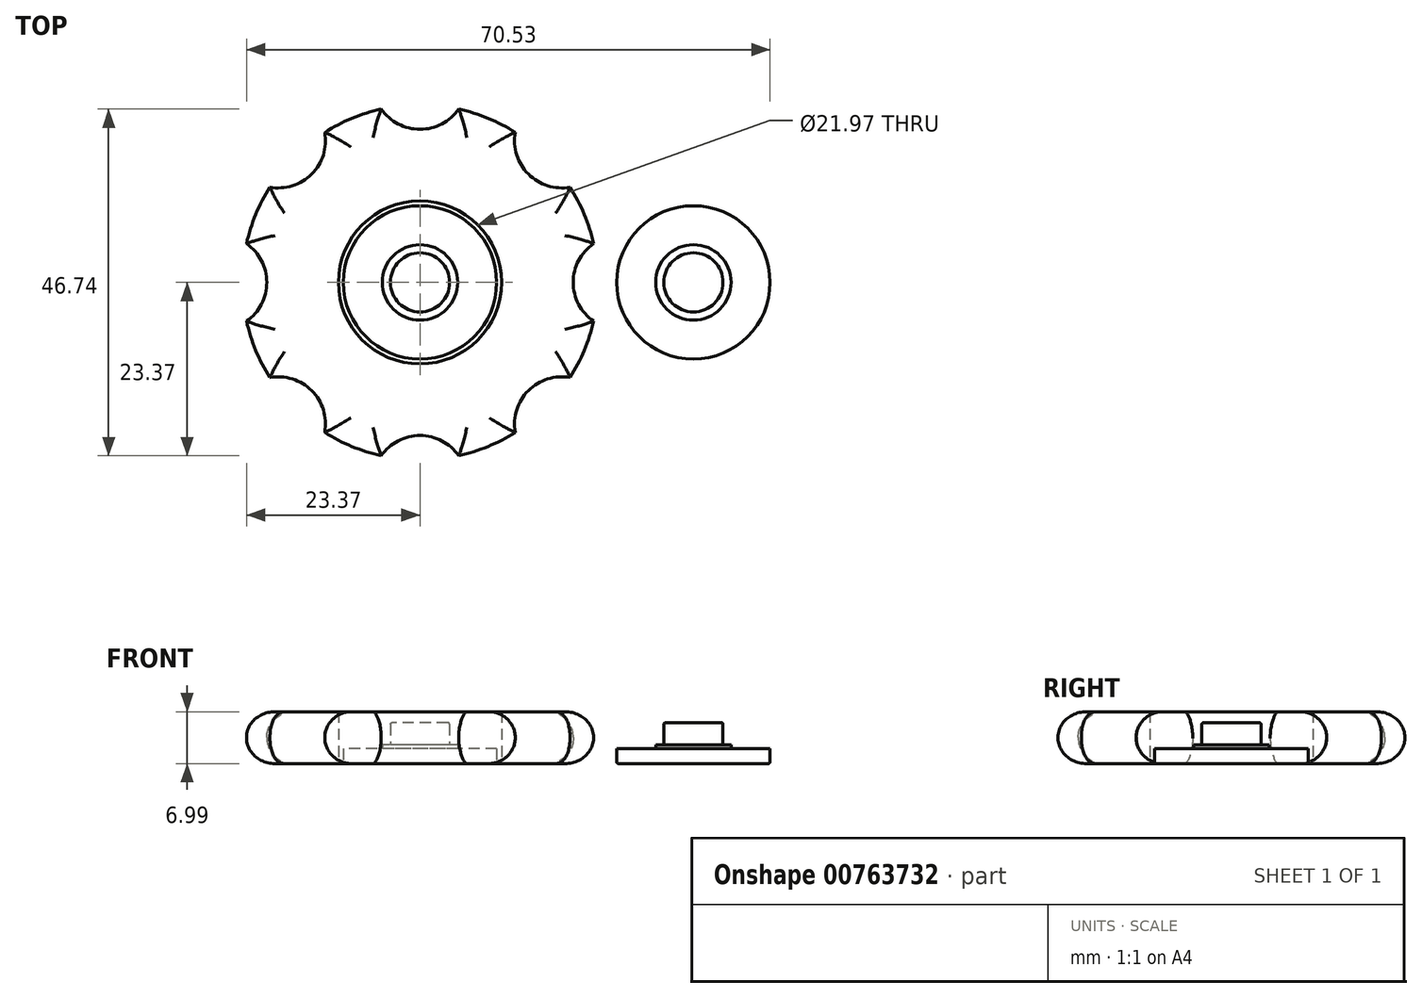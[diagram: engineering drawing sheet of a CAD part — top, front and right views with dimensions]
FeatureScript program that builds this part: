
annotation { "Feature Type Name" : "Feature", "Feature Type Description" : "" }
export const myFeature = defineFeature(function(context is Context, id is Id, definition is map)
    precondition{}
    {
        {
            var Q0;
            Q0=qCreatedBy(makeId("Top.planeOp"),FACE);
            var sketch = newSketch(context, id + "F0", { "sketchPlane" : qUnion([Q0])});
            skCircle(sketch, "E0", {"center": v(0, 0) * mm, "radius": 10.99 * mm});
            skCircle(sketch, "E1", {"center": v(0, 0) * mm, "radius": 26.99 * mm});
            skPoint(sketch, "E2", {"position": v(0, 26.99) * mm});
            skPoint(sketch, "E3", {"position": v(0, -26.99) * mm});
            skPoint(sketch, "E4", {"position": v(-26.99, 0) * mm});
            skPoint(sketch, "E5", {"position": v(26.99, 0) * mm});
            skCircle(sketch, "E6", {"center": v(0, 26.99) * mm, "radius": 6.35 * mm});
            skCircle(sketch, "E7", {"center": v(19.08, 19.08) * mm, "radius": 6.35 * mm});
            skCircle(sketch, "E8", {"center": v(26.99, 0) * mm, "radius": 6.35 * mm});
            skCircle(sketch, "E9", {"center": v(-19.08, 19.08) * mm, "radius": 6.35 * mm});
            skCircle(sketch, "E10", {"center": v(-26.99, 0) * mm, "radius": 6.35 * mm});
            skCircle(sketch, "E11", {"center": v(-19.08, -19.08) * mm, "radius": 6.35 * mm});
            skCircle(sketch, "E12", {"center": v(0, -26.99) * mm, "radius": 6.35 * mm});
            skCircle(sketch, "E13", {"center": v(19.08, -19.08) * mm, "radius": 6.35 * mm});
            skCircle(sketch, "E14", {"center": v(0, 0) * mm, "radius": 23.95 * mm});
            skCircle(sketch, "E15", {"center": v(0, 0) * mm, "radius": 10.33 * mm});
            skCircle(sketch, "E16", {"center": v(0, 0) * mm, "radius": 5.08 * mm});
            skCircle(sketch, "E17", {"center": v(0, 0) * mm, "radius": 3.99 * mm});
            skSolve(sketch);
        }
        {
            var Q0;
            {var subQ1=sQuery(id+"F0.wireOp",EDGE,"vauF7w1j-dYiE-ONAp-yt3V-veebpfeqqCza");var subQ6=sQuery(id+"F0.wireOp",EDGE,"E0");var subQ11=makeQuery(id+"F0.imprint","INTERSECT",VERTEX,{"disambiguationData":[OD(0.0)],"derivedFrom":[subQ6,subQ1]});Q0=makeQuery(id+"F0.imprint","IMPRINT",FACE,{"disambiguationData":[TD([[makeQuery(id+"F0.imprint","IMPRINT",EDGE,{"disambiguationData":[TD([[subQ11,-1.0]])],"derivedFrom":subQ6}),-1.0]])]});}
            var Q1;
            {var subQ1=sQuery(id+"F0.wireOp",EDGE,"2xs85ny7-f9sM-EysO-I2VY-nclEqGJr2pPz");var subQ6=sQuery(id+"F0.wireOp",EDGE,"E0");var subQ10=makeQuery(id+"F0.imprint","INTERSECT",VERTEX,{"disambiguationData":[OD(0.0)],"derivedFrom":[subQ6,subQ1]});Q1=makeQuery(id+"F0.imprint","IMPRINT",FACE,{"disambiguationData":[TD([[makeQuery(id+"F0.imprint","IMPRINT",EDGE,{"disambiguationData":[TD([[subQ10,-1.0]])],"derivedFrom":subQ6}),-1.0]])]});}
            var Q2;
            {var subQ0=sQuery(id+"F0.wireOp",EDGE,"xx3eZdgf-G35K-R4WY-AsTk-CgdW70iCga0P");var subQ1=sQuery(id+"F0.wireOp",EDGE,"E0");var subQ2=makeQuery(id+"F0.imprint","INTERSECT",VERTEX,{"disambiguationData":[OD(0.0)],"derivedFrom":[subQ1,subQ0]});Q2=makeQuery(id+"F0.imprint","IMPRINT",FACE,{"disambiguationData":[TD([[makeQuery(id+"F0.imprint","IMPRINT",EDGE,{"disambiguationData":[TD([[subQ2,-1.0]])],"derivedFrom":subQ1}),-1.0]])]});}
            var Q3;
            {var subQ1=sQuery(id+"F0.wireOp",EDGE,"xx3eZdgf-G35K-R4WY-AsTk-CgdW70iCga0P");var subQ5=sQuery(id+"F0.wireOp",EDGE,"E0");var subQ6=makeQuery(id+"F0.imprint","INTERSECT",VERTEX,{"disambiguationData":[OD(0.0)],"derivedFrom":[subQ5,subQ1]});Q3=makeQuery(id+"F0.imprint","IMPRINT",FACE,{"disambiguationData":[TD([[makeQuery(id+"F0.imprint","IMPRINT",EDGE,{"disambiguationData":[TD([[subQ6,1.0]])],"derivedFrom":subQ5}),-1.0]])]});}
            var Q4;
            {var subQ1=sQuery(id+"F0.wireOp",EDGE,"aaSnfk4t-Vx8F-0rh1-x5wZ-IxOcUmj5yS2X");var subQ6=sQuery(id+"F0.wireOp",EDGE,"E0");var subQ10=makeQuery(id+"F0.imprint","INTERSECT",VERTEX,{"disambiguationData":[OD(0.0)],"derivedFrom":[subQ6,subQ1]});Q4=makeQuery(id+"F0.imprint","IMPRINT",FACE,{"disambiguationData":[TD([[makeQuery(id+"F0.imprint","IMPRINT",EDGE,{"disambiguationData":[TD([[subQ10,1.0]])],"derivedFrom":subQ6}),-1.0]])]});}
            var Q5;
            {var subQ1=sQuery(id+"F0.wireOp",EDGE,"2xs85ny7-f9sM-EysO-I2VY-nclEqGJr2pPz");var subQ5=sQuery(id+"F0.wireOp",EDGE,"E0");var subQ6=makeQuery(id+"F0.imprint","INTERSECT",VERTEX,{"disambiguationData":[OD(1.0)],"derivedFrom":[subQ5,subQ1]});Q5=makeQuery(id+"F0.imprint","IMPRINT",FACE,{"disambiguationData":[TD([[makeQuery(id+"F0.imprint","IMPRINT",EDGE,{"disambiguationData":[TD([[subQ6,-1.0]])],"derivedFrom":subQ5}),-1.0]])]});}
            var Q6;
            {var subQ1=sQuery(id+"F0.wireOp",EDGE,"xx3eZdgf-G35K-R4WY-AsTk-CgdW70iCga0P");var subQ5=sQuery(id+"F0.wireOp",EDGE,"E0");var subQ6=makeQuery(id+"F0.imprint","INTERSECT",VERTEX,{"disambiguationData":[OD(1.0)],"derivedFrom":[subQ5,subQ1]});Q6=makeQuery(id+"F0.imprint","IMPRINT",FACE,{"disambiguationData":[TD([[makeQuery(id+"F0.imprint","IMPRINT",EDGE,{"disambiguationData":[TD([[subQ6,-1.0]])],"derivedFrom":subQ5}),-1.0]])]});}
            var Q7;
            {var subQ1=sQuery(id+"F0.wireOp",EDGE,"aaSnfk4t-Vx8F-0rh1-x5wZ-IxOcUmj5yS2X");var subQ6=sQuery(id+"F0.wireOp",EDGE,"E0");var subQ10=makeQuery(id+"F0.imprint","INTERSECT",VERTEX,{"disambiguationData":[OD(1.0)],"derivedFrom":[subQ6,subQ1]});Q7=makeQuery(id+"F0.imprint","IMPRINT",FACE,{"disambiguationData":[TD([[makeQuery(id+"F0.imprint","IMPRINT",EDGE,{"disambiguationData":[TD([[subQ10,-1.0]])],"derivedFrom":subQ6}),-1.0]])]});}
            extrude(context, id + "F1", {"entities" : qUnion([Q0, Q1, Q2, Q3, Q4, Q5, Q6, Q7]), "depth" : 7 * mm, "offsetDistance" : 25.4 * mm});
        }
        {
            var Q0;
            Q0=makeQuery(id+"F1.opExtrude","CAP_EDGE",EDGE,{"disambiguationData":[OSD([sQuery(id+"F0.wireOp",EDGE,"E10")])],"isStart":false});
            var Q1;
            Q1=makeQuery(id+"F1.opExtrude","CAP_EDGE",EDGE,{"disambiguationData":[OSD([sQuery(id+"F0.wireOp",EDGE,"E9")])],"isStart":false});
            var Q2;
            Q2=makeQuery(id+"F1.opExtrude","CAP_EDGE",EDGE,{"disambiguationData":[OSD([sQuery(id+"F0.wireOp",EDGE,"E6")])],"isStart":false});
            var Q3;
            Q3=makeQuery(id+"F1.opExtrude","CAP_EDGE",EDGE,{"disambiguationData":[OSD([sQuery(id+"F0.wireOp",EDGE,"E7")])],"isStart":false});
            var Q4;
            Q4=makeQuery(id+"F1.opExtrude","CAP_EDGE",EDGE,{"disambiguationData":[OSD([sQuery(id+"F0.wireOp",EDGE,"E8")])],"isStart":false});
            var Q5;
            Q5=makeQuery(id+"F1.opExtrude","CAP_EDGE",EDGE,{"disambiguationData":[OSD([sQuery(id+"F0.wireOp",EDGE,"E13")])],"isStart":false});
            var Q6;
            Q6=makeQuery(id+"F1.opExtrude","CAP_EDGE",EDGE,{"disambiguationData":[OSD([sQuery(id+"F0.wireOp",EDGE,"E12")])],"isStart":false});
            var Q7;
            {var subQ0=sQuery(id+"F0.wireOp",EDGE,"E14");Q7=makeQuery(id+"F1.opExtrude","CAP_EDGE",EDGE,{"disambiguationData":[OSD([subQ0]),TDD([makeQuery(id+"F0.imprint","IMPRINT",EDGE,{"disambiguationData":[TD([[makeQuery(id+"F0.imprint","INTERSECT",VERTEX,{"disambiguationData":[OD(0.0)],"derivedFrom":[sQuery(id+"F0.wireOp",EDGE,"E12"),subQ0]}),-1.0]])],"derivedFrom":subQ0})])],"isStart":false});}
            var Q8;
            {var subQ0=sQuery(id+"F0.wireOp",EDGE,"E14");Q8=makeQuery(id+"F1.opExtrude","CAP_EDGE",EDGE,{"disambiguationData":[OSD([subQ0]),TDD([makeQuery(id+"F0.imprint","IMPRINT",EDGE,{"disambiguationData":[TD([[makeQuery(id+"F0.imprint","INTERSECT",VERTEX,{"disambiguationData":[OD(1.0)],"derivedFrom":[sQuery(id+"F0.wireOp",EDGE,"E11"),subQ0]}),-1.0]])],"derivedFrom":subQ0})])],"isStart":false});}
            var Q9;
            Q9=makeQuery(id+"F1.opExtrude","CAP_EDGE",EDGE,{"disambiguationData":[OSD([sQuery(id+"F0.wireOp",EDGE,"E11")])],"isStart":false});
            var Q10;
            {var subQ0=sQuery(id+"F0.wireOp",EDGE,"E14");Q10=makeQuery(id+"F1.opExtrude","CAP_EDGE",EDGE,{"disambiguationData":[OSD([subQ0]),TDD([makeQuery(id+"F0.imprint","IMPRINT",EDGE,{"disambiguationData":[TD([[makeQuery(id+"F0.imprint","INTERSECT",VERTEX,{"disambiguationData":[OD(1.0)],"derivedFrom":[sQuery(id+"F0.wireOp",EDGE,"E10"),subQ0]}),-1.0]])],"derivedFrom":subQ0})])],"isStart":false});}
            var Q11;
            {var subQ0=sQuery(id+"F0.wireOp",EDGE,"E14");Q11=makeQuery(id+"F1.opExtrude","CAP_EDGE",EDGE,{"disambiguationData":[OSD([subQ0]),TDD([makeQuery(id+"F0.imprint","IMPRINT",EDGE,{"disambiguationData":[TD([[makeQuery(id+"F0.imprint","INTERSECT",VERTEX,{"disambiguationData":[OD(1.0)],"derivedFrom":[sQuery(id+"F0.wireOp",EDGE,"E9"),subQ0]}),-1.0]])],"derivedFrom":subQ0})])],"isStart":false});}
            var Q12;
            {var subQ0=sQuery(id+"F0.wireOp",EDGE,"E14");Q12=makeQuery(id+"F1.opExtrude","CAP_EDGE",EDGE,{"disambiguationData":[OSD([subQ0]),TDD([makeQuery(id+"F0.imprint","IMPRINT",EDGE,{"disambiguationData":[TD([[makeQuery(id+"F0.imprint","INTERSECT",VERTEX,{"disambiguationData":[OD(0.0)],"derivedFrom":[sQuery(id+"F0.wireOp",EDGE,"E6"),subQ0]}),-1.0]])],"derivedFrom":subQ0})])],"isStart":false});}
            var Q13;
            {var subQ0=sQuery(id+"F0.wireOp",EDGE,"E14");Q13=makeQuery(id+"F1.opExtrude","CAP_EDGE",EDGE,{"disambiguationData":[OSD([subQ0]),TDD([makeQuery(id+"F0.imprint","IMPRINT",EDGE,{"disambiguationData":[TD([[makeQuery(id+"F0.imprint","INTERSECT",VERTEX,{"disambiguationData":[OD(1.0)],"derivedFrom":[sQuery(id+"F0.wireOp",EDGE,"E6"),subQ0]}),1.0]])],"derivedFrom":subQ0})])],"isStart":false});}
            var Q14;
            {var subQ0=sQuery(id+"F0.wireOp",EDGE,"E14");Q14=makeQuery(id+"F1.opExtrude","CAP_EDGE",EDGE,{"disambiguationData":[OSD([subQ0]),TDD([makeQuery(id+"F0.imprint","IMPRINT",EDGE,{"disambiguationData":[TD([[makeQuery(id+"F0.imprint","INTERSECT",VERTEX,{"disambiguationData":[OD(1.0)],"derivedFrom":[sQuery(id+"F0.wireOp",EDGE,"E7"),subQ0]}),1.0]])],"derivedFrom":subQ0})])],"isStart":false});}
            var Q15;
            {var subQ0=sQuery(id+"F0.wireOp",EDGE,"E14");Q15=makeQuery(id+"F1.opExtrude","CAP_EDGE",EDGE,{"disambiguationData":[OSD([subQ0]),TDD([makeQuery(id+"F0.imprint","IMPRINT",EDGE,{"disambiguationData":[TD([[makeQuery(id+"F0.imprint","INTERSECT",VERTEX,{"disambiguationData":[OD(1.0)],"derivedFrom":[sQuery(id+"F0.wireOp",EDGE,"E8"),subQ0]}),1.0]])],"derivedFrom":subQ0})])],"isStart":false});}
            var Q16;
            {var subQ0=sQuery(id+"F0.wireOp",EDGE,"E14");Q16=makeQuery(id+"F1.opExtrude","CAP_EDGE",EDGE,{"disambiguationData":[OSD([subQ0]),TDD([makeQuery(id+"F0.imprint","IMPRINT",EDGE,{"disambiguationData":[TD([[makeQuery(id+"F0.imprint","INTERSECT",VERTEX,{"disambiguationData":[OD(1.0)],"derivedFrom":[sQuery(id+"F0.wireOp",EDGE,"E11"),subQ0]}),-1.0]])],"derivedFrom":subQ0})])],"isStart":true});}
            var Q17;
            Q17=makeQuery(id+"F1.opExtrude","CAP_EDGE",EDGE,{"disambiguationData":[OSD([sQuery(id+"F0.wireOp",EDGE,"E11")])],"isStart":true});
            var Q18;
            {var subQ0=sQuery(id+"F0.wireOp",EDGE,"E14");Q18=makeQuery(id+"F1.opExtrude","CAP_EDGE",EDGE,{"disambiguationData":[OSD([subQ0]),TDD([makeQuery(id+"F0.imprint","IMPRINT",EDGE,{"disambiguationData":[TD([[makeQuery(id+"F0.imprint","INTERSECT",VERTEX,{"disambiguationData":[OD(1.0)],"derivedFrom":[sQuery(id+"F0.wireOp",EDGE,"E10"),subQ0]}),-1.0]])],"derivedFrom":subQ0})])],"isStart":true});}
            var Q19;
            Q19=makeQuery(id+"F1.opExtrude","CAP_EDGE",EDGE,{"disambiguationData":[OSD([sQuery(id+"F0.wireOp",EDGE,"E10")])],"isStart":true});
            var Q20;
            {var subQ0=sQuery(id+"F0.wireOp",EDGE,"E14");Q20=makeQuery(id+"F1.opExtrude","CAP_EDGE",EDGE,{"disambiguationData":[OSD([subQ0]),TDD([makeQuery(id+"F0.imprint","IMPRINT",EDGE,{"disambiguationData":[TD([[makeQuery(id+"F0.imprint","INTERSECT",VERTEX,{"disambiguationData":[OD(1.0)],"derivedFrom":[sQuery(id+"F0.wireOp",EDGE,"E9"),subQ0]}),-1.0]])],"derivedFrom":subQ0})])],"isStart":true});}
            var Q21;
            Q21=makeQuery(id+"F1.opExtrude","CAP_EDGE",EDGE,{"disambiguationData":[OSD([sQuery(id+"F0.wireOp",EDGE,"E9")])],"isStart":true});
            var Q22;
            {var subQ0=sQuery(id+"F0.wireOp",EDGE,"E14");Q22=makeQuery(id+"F1.opExtrude","CAP_EDGE",EDGE,{"disambiguationData":[OSD([subQ0]),TDD([makeQuery(id+"F0.imprint","IMPRINT",EDGE,{"disambiguationData":[TD([[makeQuery(id+"F0.imprint","INTERSECT",VERTEX,{"disambiguationData":[OD(0.0)],"derivedFrom":[sQuery(id+"F0.wireOp",EDGE,"E6"),subQ0]}),-1.0]])],"derivedFrom":subQ0})])],"isStart":true});}
            var Q23;
            Q23=makeQuery(id+"F1.opExtrude","CAP_EDGE",EDGE,{"disambiguationData":[OSD([sQuery(id+"F0.wireOp",EDGE,"E6")])],"isStart":true});
            var Q24;
            {var subQ0=sQuery(id+"F0.wireOp",EDGE,"E14");Q24=makeQuery(id+"F1.opExtrude","CAP_EDGE",EDGE,{"disambiguationData":[OSD([subQ0]),TDD([makeQuery(id+"F0.imprint","IMPRINT",EDGE,{"disambiguationData":[TD([[makeQuery(id+"F0.imprint","INTERSECT",VERTEX,{"disambiguationData":[OD(1.0)],"derivedFrom":[sQuery(id+"F0.wireOp",EDGE,"E6"),subQ0]}),1.0]])],"derivedFrom":subQ0})])],"isStart":true});}
            var Q25;
            Q25=makeQuery(id+"F1.opExtrude","CAP_EDGE",EDGE,{"disambiguationData":[OSD([sQuery(id+"F0.wireOp",EDGE,"E12")])],"isStart":true});
            var Q26;
            {var subQ0=sQuery(id+"F0.wireOp",EDGE,"E14");Q26=makeQuery(id+"F1.opExtrude","CAP_EDGE",EDGE,{"disambiguationData":[OSD([subQ0]),TDD([makeQuery(id+"F0.imprint","IMPRINT",EDGE,{"disambiguationData":[TD([[makeQuery(id+"F0.imprint","INTERSECT",VERTEX,{"disambiguationData":[OD(0.0)],"derivedFrom":[sQuery(id+"F0.wireOp",EDGE,"E12"),subQ0]}),-1.0]])],"derivedFrom":subQ0})])],"isStart":true});}
            var Q27;
            Q27=makeQuery(id+"F1.opExtrude","CAP_EDGE",EDGE,{"disambiguationData":[OSD([sQuery(id+"F0.wireOp",EDGE,"E13")])],"isStart":true});
            var Q28;
            {var subQ0=sQuery(id+"F0.wireOp",EDGE,"E14");Q28=makeQuery(id+"F1.opExtrude","CAP_EDGE",EDGE,{"disambiguationData":[OSD([subQ0]),TDD([makeQuery(id+"F0.imprint","IMPRINT",EDGE,{"disambiguationData":[TD([[makeQuery(id+"F0.imprint","INTERSECT",VERTEX,{"disambiguationData":[OD(1.0)],"derivedFrom":[sQuery(id+"F0.wireOp",EDGE,"E8"),subQ0]}),1.0]])],"derivedFrom":subQ0})])],"isStart":true});}
            var Q29;
            Q29=makeQuery(id+"F1.opExtrude","CAP_EDGE",EDGE,{"disambiguationData":[OSD([sQuery(id+"F0.wireOp",EDGE,"E8")])],"isStart":true});
            var Q30;
            {var subQ0=sQuery(id+"F0.wireOp",EDGE,"E14");Q30=makeQuery(id+"F1.opExtrude","CAP_EDGE",EDGE,{"disambiguationData":[OSD([subQ0]),TDD([makeQuery(id+"F0.imprint","IMPRINT",EDGE,{"disambiguationData":[TD([[makeQuery(id+"F0.imprint","INTERSECT",VERTEX,{"disambiguationData":[OD(1.0)],"derivedFrom":[sQuery(id+"F0.wireOp",EDGE,"E7"),subQ0]}),1.0]])],"derivedFrom":subQ0})])],"isStart":true});}
            var Q31;
            Q31=makeQuery(id+"F1.opExtrude","CAP_EDGE",EDGE,{"disambiguationData":[OSD([sQuery(id+"F0.wireOp",EDGE,"E7")])],"isStart":true});
            fillet(context, id + "F2", {"entities" : qUnion([Q0, Q1, Q2, Q3, Q4, Q5, Q6, Q7, Q8, Q9, Q10, Q11, Q12, Q13, Q14, Q15, Q16, Q17, Q18, Q19, Q20, Q21, Q22, Q23, Q24, Q25, Q26, Q27, Q28, Q29, Q30, Q31]), "radius" : 3.43 * mm, "tangentPropagation" : true, "allowEdgeOverflow" : false});
        }
        {
            var Q0;
            Q0=makeQuery(id+"F0.imprint","IMPRINT",FACE,{"disambiguationData":[TD([[makeQuery(id+"F0.imprint","IMPRINT",EDGE,{"derivedFrom":sQuery(id+"F0.wireOp",EDGE,"E15")}),1.0]])]});
            extrude(context, id + "F3", {"entities" : qUnion([Q0]), "depth" : 1.98 * mm, "offsetDistance" : 25.4 * mm});
        }
        {
            var Q0;
            Q0=makeQuery(id+"F0.imprint","IMPRINT",FACE,{"disambiguationData":[TD([[makeQuery(id+"F0.imprint","IMPRINT",EDGE,{"derivedFrom":sQuery(id+"F0.wireOp",EDGE,"E16")}),1.0]])]});
            extrude(context, id + "F4", {"entities" : qUnion([Q0]), "operationType" : NewBodyOperationType.ADD, "depth" : 2.54 * mm, "offsetDistance" : 25.4 * mm});
        }
        {
            var Q0;
            Q0=makeQuery(id+"F0.imprint","IMPRINT",FACE,{"disambiguationData":[TD([[makeQuery(id+"F0.imprint","IMPRINT",EDGE,{"derivedFrom":sQuery(id+"F0.wireOp",EDGE,"E17")}),1.0]])]});
            extrude(context, id + "F5", {"entities" : qUnion([Q0]), "operationType" : NewBodyOperationType.ADD, "depth" : 5.5 * mm, "offsetDistance" : 25.4 * mm});
        }
        {
            var Q0;
            Q0=makeQuery(id+"F3.opExtrude","CAP_EDGE",EDGE,{"disambiguationData":[OSD([sQuery(id+"F0.wireOp",EDGE,"E15")])],"isStart":true});
            var Q1;
            Q1=makeQuery(id+"F5.opExtrude","CAP_EDGE",EDGE,{"disambiguationData":[OSD([sQuery(id+"F0.wireOp",EDGE,"E17")])],"isStart":false});
            fillet(context, id + "F6", {"entities" : qUnion([Q0, Q1]), "radius" : 0.23 * mm, "tangentPropagation" : true, "allowEdgeOverflow" : false});
        }
        {
            var Q0;
            Q0=makeQuery(id+"F3.opExtrude","SWEPT_BODY",BODY,{"disambiguationData":[OSD([sQuery(id+"F0.wireOp",EDGE,"E15"),sQuery(id+"F0.wireOp",EDGE,"E16")])]});
            transform(context, id + "F7", {"entities" : qUnion([Q0]), "transformType" : TransformType.TRANSLATION_3D, "dx" : 36.83 * mm, "dy" : 0 * mm, "dz" : 0 * mm, "makeCopy" : true});
        }
    });
